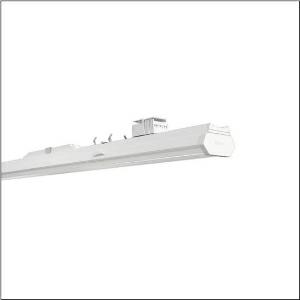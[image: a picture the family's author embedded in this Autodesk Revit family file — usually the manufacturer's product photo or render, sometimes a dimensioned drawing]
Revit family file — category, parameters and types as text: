
# Revit family: licross_r__21_protected_mo_52td11vn48xgd_36f3
name_source: partatom
category: Lighting Fixtures
units: mm (PartAtom-declared; Revit-internal decimal feet)

## family parameters
Cut with Voids When Loaded = No
Host = Face
Light Source = No
Part Type = Normal
Room Calculation Point = No
Round Connector Dimension = Use Diameter
Shared = No

## types (1)
- --- (1 x LED, 980 lm, 7 W, 4000K)
    Apparent Load = 7 VA
    CIE Flux Codes = 83 94 98 100 100
    Color Rendering = 80
    Color Temperature = 4000K
    Default Elevation = 1800 mm
    Description = Licross® 21 Protected MO, luminaire insert, of sheet steel, galvanised, coil coated, white, length: 1.500mm, width: 90mm, height: 103mm, LED rated luminous flux: 8.000lm, light colour: 840, control gear: DALI 2, CLO (for two DALI lines), with plug, 6-pole, with phase selection, mains connection: 220..240V, AC/DC, 0/50..60Hz, start of lifetime: 46W, end of service life: 52W, without changeover relay, for emergency light function, for central battery installations according to DIN EN 60598-2-22, internal wiring halogen-free, primary optical cover: cover, of PMMA, light emission: direct distribution, primary light characteristic: symmetric, protection rating (complete): IP54, insulation class (complete): insulation class I (protective earthing), certification: CE, ENEC, VDE, UKCA, protection symbol: D if used in an environment with non-conductive dust loads with corresponding accessories, impact resistance: IK06, permissible ambient temperature for indoor applications: -25..+50°C, standard: EN 60598-2-22, corresponds to IFS (International Featured Standards) requirements for safety and quality in the food industry, reducing of maximum allowable ambient temperature of 5°C with ceiling mounting, LABS conformity tested according to VDMA 24364:2018-05, packaging unit: 1 piece
    Height = 92 mm
    Lamp = 1 x LED
    Lamp Light Flux = 980 lm
    Lamp Power = 7 W
    Lamp count = 1
    Length = 1500 mm
    Luminous efficacy = 140 lm/W
    Manufacturer = Siteco
    ModVariant = No
    Model = 52TD11VN48XGD
    Mounting Place = Ceiling
    Mounting Type = Pendant
    Number of Poles = 1
    OnlyDefault = Yes
    Power Factor = 1
    Product Name = Licross® 21 Protected MO
    Product group = luminaire insert | ceiling pendant
    ProductGroupID = 902
    Protection Class = Protection class I
    Protection Degree = IP 54
    RLX_Detail_Level = 1
    RLX_Emergency_Light_Flux = 0 lm
    RLX_Emergency_Type = 0
    RLX_Emergency_Type_DB = No
    RlxData = <blob elided: 24585 chars, md5=9f8e9512>
    Socket = socket
    Standby Power = 0 W
    System Light Flux = 980 lm
    System Power = 7 W
    Type Comments = : DC mode (central or group accumulator) initial emergency light level
    Type Image = l_1256148.jpg
    URL = http://relux.com
    VarID = @adj_104131
    Voltage = 0 V
    Weight = 0.00 kg
    Width = 88 mm

## geometry (parser evidence)
native form markers: Blend x4, Sweep x10
no freeform markers — native parametric forms only
